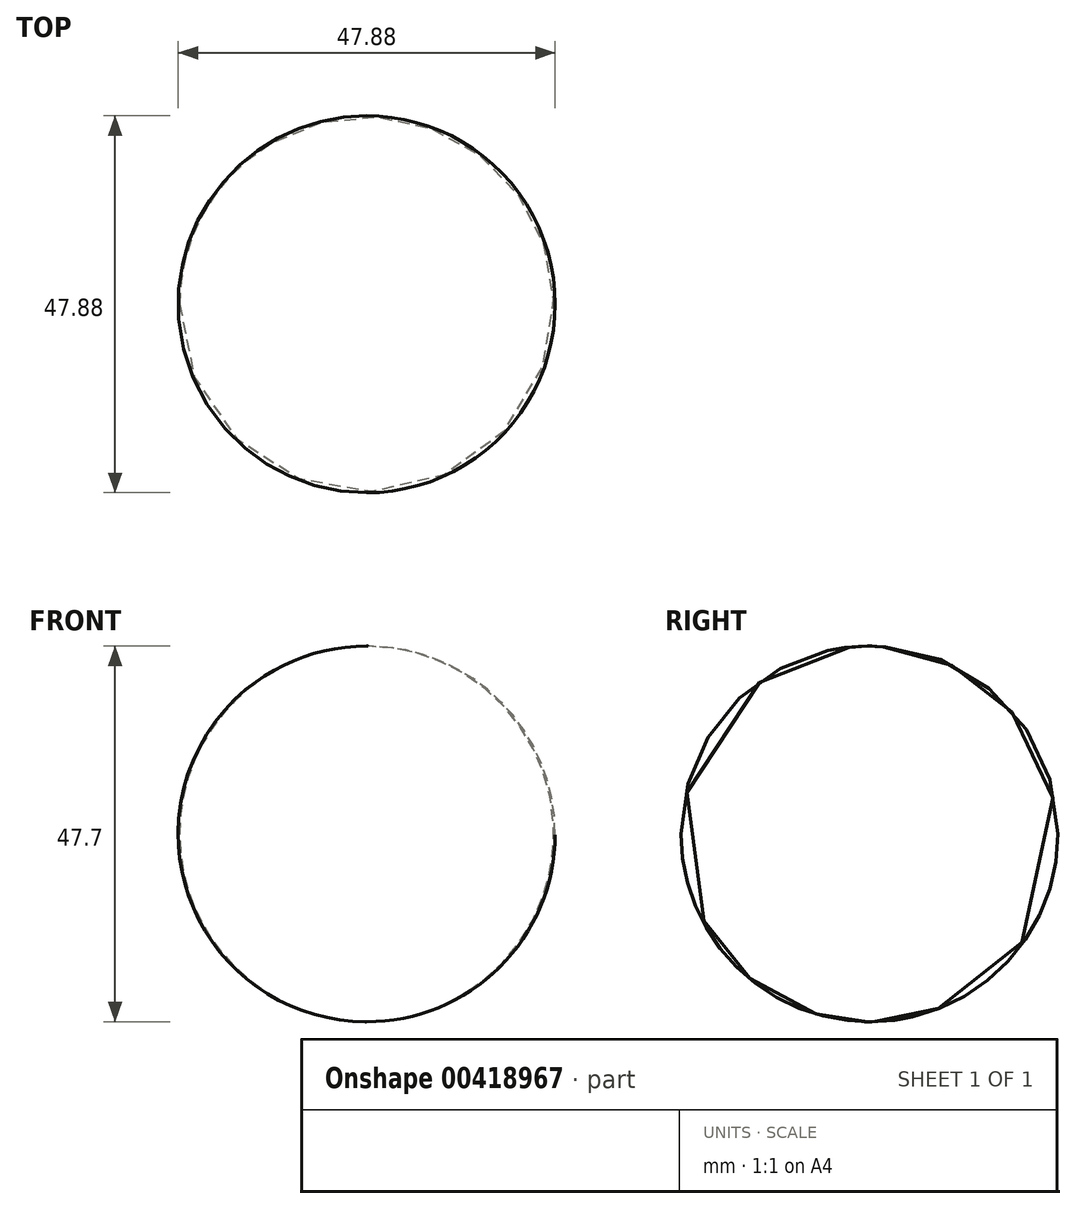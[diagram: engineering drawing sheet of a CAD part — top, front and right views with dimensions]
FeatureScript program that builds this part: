
annotation { "Feature Type Name" : "Feature", "Feature Type Description" : "" }
export const myFeature = defineFeature(function(context is Context, id is Id, definition is map)
    precondition{}
    {
        {
            var Q0;
            Q0=qCreatedBy(makeId("Front.planeOp"),FACE);
            var sketch = newSketch(context, id + "F0", { "sketchPlane" : qUnion([Q0])});
            skArc(sketch, "E0", {"start": v(0.02, 23.85) * mm, "mid": v(-23.85, 0.1) * mm, "end": v(-0.2, -23.85) * mm});
            skLineSegment(sketch, "E1", {"start": v(0.02, 23.85) * mm, "end": v(-0.2, -23.85) * mm});
            skSolve(sketch);
        }
        {
            var Q0;
            Q0 = qSketchRegion(id + "F0", true);
            var Q1;
            Q1=sQuery(id+"F0.wireOp",EDGE,"E1");
            revolve(context, id + "F1", {"entities" : qUnion([Q0]), "axis" : qUnion([Q1]), "revolveType" : RevolveType.FULL});
        }
    });
